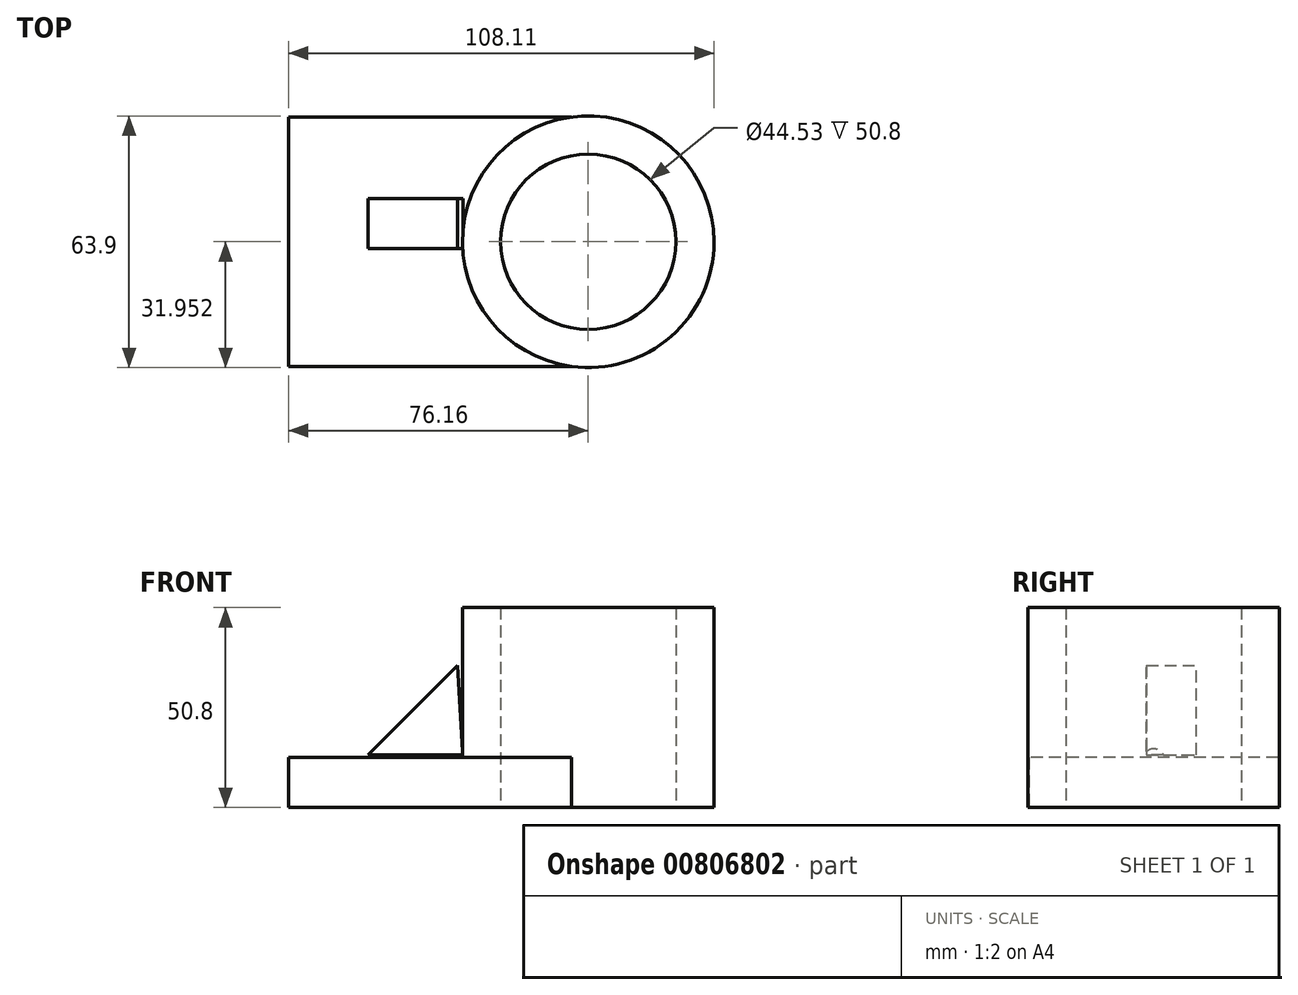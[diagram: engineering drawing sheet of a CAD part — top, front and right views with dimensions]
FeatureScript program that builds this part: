
annotation { "Feature Type Name" : "Feature", "Feature Type Description" : "" }
export const myFeature = defineFeature(function(context is Context, id is Id, definition is map)
    precondition{}
    {
        {
            var Q0;
            Q0=qCreatedBy(makeId("Top.planeOp"),FACE);
            var sketch = newSketch(context, id + "F0", { "sketchPlane" : qUnion([Q0])});
            skLineSegment(sketch, "E0.bottom", {"start": v(38.08, 27.1) * mm, "end": v(-38.08, 27.1) * mm});
            skLineSegment(sketch, "E0.top", {"start": v(38.08, -36.23) * mm, "end": v(-38.08, -36.23) * mm});
            skLineSegment(sketch, "E0.left", {"start": v(38.08, 27.1) * mm, "end": v(38.08, -36.23) * mm});
            skLineSegment(sketch, "E0.right", {"start": v(-38.08, 27.1) * mm, "end": v(-38.08, -36.23) * mm});
            skPoint(sketch, "E0.middle", {"position": v(0, -4.57) * mm});
            skCircle(sketch, "E1", {"center": v(38.08, -4.57) * mm, "radius": 31.95 * mm});
            skCircle(sketch, "E2", {"center": v(38.08, -4.57) * mm, "radius": 22.27 * mm});
            skSolve(sketch);
        }
        {
            var Q0;
            {var subQ0=sQuery(id+"F0.wireOp",EDGE,"E0.left");var subQ5=sQuery(id+"F0.wireOp",EDGE,"E0.bottom");var subQ6=makeQuery(id+"F0.imprint","INTERSECT",VERTEX,{"derivedFrom":[subQ5,subQ0]});Q0=makeQuery(id+"F0.imprint","IMPRINT",FACE,{"disambiguationData":[TD([[makeQuery(id+"F0.imprint","IMPRINT",EDGE,{"disambiguationData":[TD([[subQ6,-1.0]])],"derivedFrom":subQ5}),-1.0]])]});}
            var Q1;
            {var subQ0=sQuery(id+"F0.wireOp",EDGE,"E0.left");var subQ5=sQuery(id+"F0.wireOp",EDGE,"E0.bottom");var subQ6=makeQuery(id+"F0.imprint","INTERSECT",VERTEX,{"derivedFrom":[subQ5,subQ0]});Q1=makeQuery(id+"F0.imprint","IMPRINT",FACE,{"disambiguationData":[TD([[makeQuery(id+"F0.imprint","IMPRINT",EDGE,{"disambiguationData":[TD([[subQ6,-1.0]])],"derivedFrom":subQ5}),1.0]])]});}
            extrude(context, id + "F1", {"entities" : qUnion([Q0, Q1]), "depth" : 50.8 * mm, "offsetDistance" : 25.4 * mm});
        }
        {
            var Q0;
            Q0 = qSketchRegion(id + "F0", true);
            extrude(context, id + "F2", {"entities" : qUnion([Q0]), "operationType" : NewBodyOperationType.ADD, "depth" : 12.7 * mm, "offsetDistance" : 25.4 * mm});
        }
        {
            var Q0;
            Q0=qCreatedBy(makeId("Front.planeOp"),FACE);
            var sketch = newSketch(context, id + "F3", { "sketchPlane" : qUnion([Q0])});
            skLineSegment(sketch, "E3", {"start": v(4.84, 36.12) * mm, "end": v(-17.86, 13.42) * mm});
            skLineSegment(sketch, "E4", {"start": v(-17.86, 13.42) * mm, "end": v(6.23, 13.42) * mm});
            skLineSegment(sketch, "E5", {"start": v(6.23, 13.42) * mm, "end": v(4.84, 36.12) * mm});
            skSolve(sketch);
        }
        {
            var Q0;
            Q0=makeQuery(id+"F3.imprint","IMPRINT",FACE,{"disambiguationData":[TD([[makeQuery(id+"F3.imprint","IMPRINT",EDGE,{"derivedFrom":sQuery(id+"F3.wireOp",EDGE,"E3")}),1.0]])]});
            extrude(context, id + "F4", {"entities" : qUnion([Q0]), "operationType" : NewBodyOperationType.ADD, "endBound" : BoundingType.SYMMETRIC, "depth" : 12.7 * mm, "offsetDistance" : 25.4 * mm});
        }
    });
